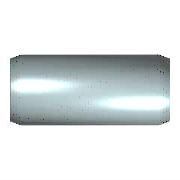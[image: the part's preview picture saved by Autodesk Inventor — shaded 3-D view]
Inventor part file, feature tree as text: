
AUTODESK INVENTOR PART (.ipt)
format: ipt  version: 2023.3 (Build 273359000, 359)  size: 115,200 bytes
history: native  units: mm (DEFAULTED — no unit token found)
features: extrude x1, chamfer x1, sketch x1
ambient origin geometry x8: Origin, YZ Plane, XZ Plane, XY Plane, X Axis, Y Axis, Z Axis, Center Point
bodies: Solid1 (feature_tree)
feature tree (3):
  extrude  "Körper"  Depth=10.0mm
  chamfer  "Skizze2"  [1 undecoded]
  sketch  "Skizze"  dims[d1=2.0mm d2=10.0mm d3=0.0mm d4=0.35mm d5=15.0deg d8=0.35mm d9=15.0deg d11=0.35mm d12=0.35mm d13=0.0mm d15=0.0mm d16=0.0mm]
note: 1 required parameter value undecoded (feature->parameter linkage not recoverable at this tier; creation-order binding heuristic only, values carry confidence <= 0.55)
